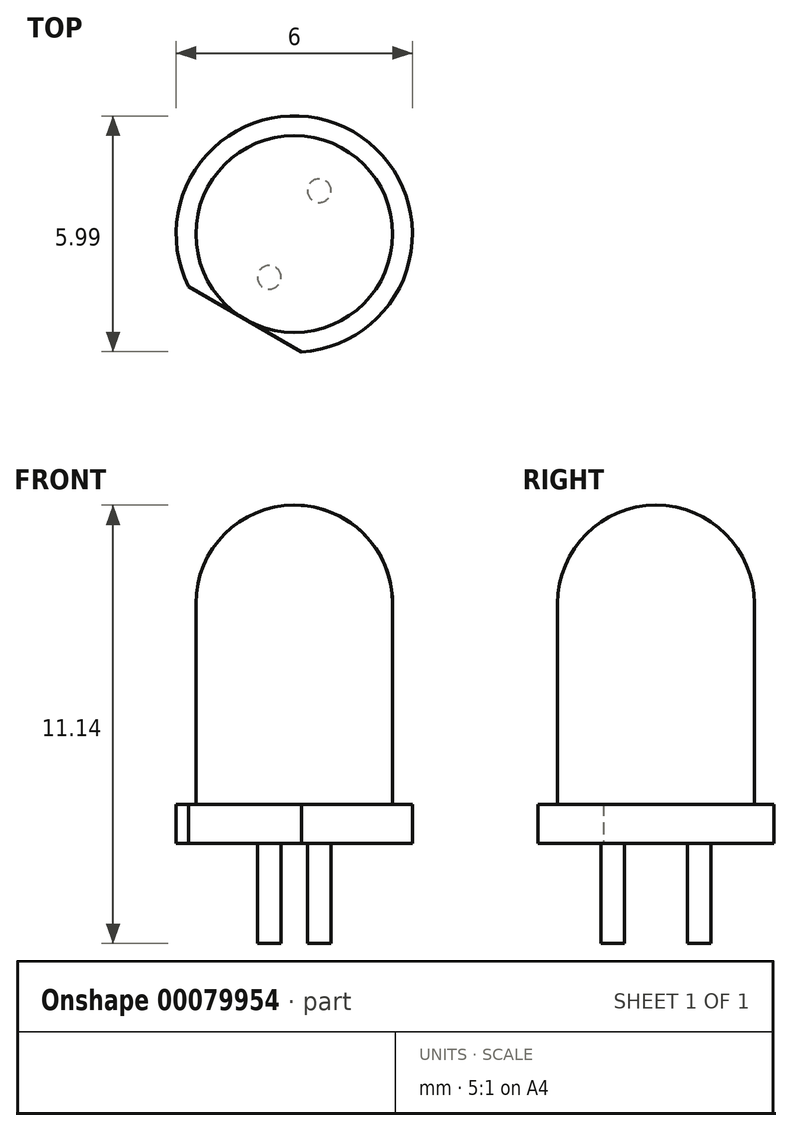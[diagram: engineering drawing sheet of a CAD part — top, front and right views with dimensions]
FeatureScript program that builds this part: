
annotation { "Feature Type Name" : "Feature", "Feature Type Description" : "" }
export const myFeature = defineFeature(function(context is Context, id is Id, definition is map)
    precondition{}
    {
        {
            var Q0;
            Q0=qCreatedBy(makeId("Top.planeOp"),FACE);
            var sketch = newSketch(context, id + "F0", { "sketchPlane" : qUnion([Q0])});
            skCircle(sketch, "E0", {"center": v(0, 0) * mm, "radius": 2.5 * mm});
            skCircle(sketch, "E1", {"center": v(0, 0) * mm, "radius": 3 * mm});
            skLineSegment(sketch, "E2", {"start": v(-1.27, 0) * mm, "end": v(1.27, 0) * mm});
            skCircle(sketch, "E3", {"center": v(-1.27, 0) * mm, "radius": 0.3 * mm});
            skCircle(sketch, "E4", {"center": v(1.27, 0) * mm, "radius": 0.3 * mm});
            skLineSegment(sketch, "E5", {"start": v(2.5, -1.66) * mm, "end": v(2.5, 1.66) * mm});
            skLineSegment(sketch, "E6", {"start": v(-2.69, -1.34) * mm, "end": v(0.18, -3) * mm});
            skLineSegment(sketch, "E7", {"start": v(-2.69, 1.34) * mm, "end": v(0.18, 3) * mm});
            skCircle(sketch, "E8", {"center": v(-0.64, -1.1) * mm, "radius": 0.3 * mm});
            skCircle(sketch, "E9", {"center": v(0.64, -1.1) * mm, "radius": 0.3 * mm});
            skCircle(sketch, "E10", {"center": v(0.64, 1.1) * mm, "radius": 0.3 * mm});
            skCircle(sketch, "E11", {"center": v(-0.64, 1.1) * mm, "radius": 0.3 * mm});
            skLineSegment(sketch, "E12", {"start": v(-0.64, -1.1) * mm, "end": v(-1.27, 0) * mm});
            skLineSegment(sketch, "E13", {"start": v(-0.64, -1.1) * mm, "end": v(0.64, -1.1) * mm});
            skLineSegment(sketch, "E14", {"start": v(0.63, -1.1) * mm, "end": v(1.27, 0) * mm});
            skLineSegment(sketch, "E15", {"start": v(1.27, 0) * mm, "end": v(0.63, 1.1) * mm});
            skLineSegment(sketch, "E16", {"start": v(-0.64, 1.1) * mm, "end": v(0.64, 1.1) * mm});
            skLineSegment(sketch, "E17", {"start": v(-0.64, 1.1) * mm, "end": v(-1.27, 0) * mm});
            skLineSegment(sketch, "E18", {"start": v(-0.64, -1.1) * mm, "end": v(0.64, 1.1) * mm});
            skLineSegment(sketch, "E19", {"start": v(-0.63, 1.1) * mm, "end": v(0.63, -1.1) * mm});
            skSolve(sketch);
        }
        {
            var Q0;
            Q0=makeQuery(id+"F0.imprint","IMPRINT",FACE,{"disambiguationData":[TD([[makeQuery(id+"F0.imprint","IMPRINT",EDGE,{"derivedFrom":sQuery(id+"F0.wireOp",EDGE,"E0")}),1.0]])]});
            var Q1;
            Q1=makeQuery(id+"F0.imprint","IMPRINT",FACE,{"disambiguationData":[TD([[makeQuery(id+"F0.imprint","IMPRINT",EDGE,{"derivedFrom":sQuery(id+"F0.wireOp",EDGE,"E3")}),1.0]])]});
            var Q2;
            Q2=makeQuery(id+"F0.imprint","IMPRINT",FACE,{"disambiguationData":[TD([[makeQuery(id+"F0.imprint","IMPRINT",EDGE,{"derivedFrom":sQuery(id+"F0.wireOp",EDGE,"E4")}),1.0]])]});
            var Q3;
            {var subQ5=sQuery(id+"F0.wireOp",EDGE,"E18");var subQ6=sQuery(id+"F0.wireOp",EDGE,"E8");var subQ7=makeQuery(id+"F0.imprint","INTERSECT",VERTEX,{"derivedFrom":[subQ6,subQ5]});Q3=makeQuery(id+"F0.imprint","IMPRINT",FACE,{"disambiguationData":[TD([[makeQuery(id+"F0.imprint","IMPRINT",EDGE,{"disambiguationData":[TD([[subQ7,1.0]])],"derivedFrom":subQ6}),-1.0]])]});}
            var Q4;
            {var subQ1=sQuery(id+"F0.wireOp",EDGE,"E3");var subQ7=sQuery(id+"F0.wireOp",EDGE,"E2");var subQ8=makeQuery(id+"F0.imprint","INTERSECT",VERTEX,{"derivedFrom":[subQ7,subQ1]});Q4=makeQuery(id+"F0.imprint","IMPRINT",FACE,{"disambiguationData":[TD([[makeQuery(id+"F0.imprint","IMPRINT",EDGE,{"disambiguationData":[TD([[subQ8,1.0]])],"derivedFrom":subQ1}),-1.0]])]});}
            var Q5;
            {var subQ0=sQuery(id+"F0.wireOp",EDGE,"E18");var subQ1=sQuery(id+"F0.wireOp",EDGE,"E8");var subQ2=makeQuery(id+"F0.imprint","INTERSECT",VERTEX,{"derivedFrom":[subQ1,subQ0]});Q5=makeQuery(id+"F0.imprint","IMPRINT",FACE,{"disambiguationData":[TD([[makeQuery(id+"F0.imprint","IMPRINT",EDGE,{"disambiguationData":[TD([[subQ2,-1.0]])],"derivedFrom":subQ1}),1.0]])]});}
            var Q6;
            {var subQ0=sQuery(id+"F0.wireOp",EDGE,"E13");var subQ1=sQuery(id+"F0.wireOp",EDGE,"E8");var subQ2=makeQuery(id+"F0.imprint","INTERSECT",VERTEX,{"derivedFrom":[subQ1,subQ0]});Q6=makeQuery(id+"F0.imprint","IMPRINT",FACE,{"disambiguationData":[TD([[makeQuery(id+"F0.imprint","IMPRINT",EDGE,{"disambiguationData":[TD([[subQ2,1.0]])],"derivedFrom":subQ1}),1.0]])]});}
            var Q7;
            {var subQ0=sQuery(id+"F0.wireOp",EDGE,"E18");var subQ1=sQuery(id+"F0.wireOp",EDGE,"E8");var subQ2=makeQuery(id+"F0.imprint","INTERSECT",VERTEX,{"derivedFrom":[subQ1,subQ0]});Q7=makeQuery(id+"F0.imprint","IMPRINT",FACE,{"disambiguationData":[TD([[makeQuery(id+"F0.imprint","IMPRINT",EDGE,{"disambiguationData":[TD([[subQ2,1.0]])],"derivedFrom":subQ1}),1.0]])]});}
            var Q8;
            {var subQ0=sQuery(id+"F0.wireOp",EDGE,"E19");var subQ1=sQuery(id+"F0.wireOp",EDGE,"E9");var subQ2=makeQuery(id+"F0.imprint","INTERSECT",VERTEX,{"derivedFrom":[subQ1,subQ0]});Q8=makeQuery(id+"F0.imprint","IMPRINT",FACE,{"disambiguationData":[TD([[makeQuery(id+"F0.imprint","IMPRINT",EDGE,{"disambiguationData":[TD([[subQ2,-1.0]])],"derivedFrom":subQ1}),1.0]])]});}
            var Q9;
            {var subQ0=sQuery(id+"F0.wireOp",EDGE,"E14");var subQ1=sQuery(id+"F0.wireOp",EDGE,"E9");var subQ2=makeQuery(id+"F0.imprint","INTERSECT",VERTEX,{"derivedFrom":[subQ1,subQ0]});Q9=makeQuery(id+"F0.imprint","IMPRINT",FACE,{"disambiguationData":[TD([[makeQuery(id+"F0.imprint","IMPRINT",EDGE,{"disambiguationData":[TD([[subQ2,1.0]])],"derivedFrom":subQ1}),1.0]])]});}
            var Q10;
            {var subQ0=sQuery(id+"F0.wireOp",EDGE,"E14");var subQ1=sQuery(id+"F0.wireOp",EDGE,"E9");var subQ2=makeQuery(id+"F0.imprint","INTERSECT",VERTEX,{"derivedFrom":[subQ1,subQ0]});Q10=makeQuery(id+"F0.imprint","IMPRINT",FACE,{"disambiguationData":[TD([[makeQuery(id+"F0.imprint","IMPRINT",EDGE,{"disambiguationData":[TD([[subQ2,1.0]])],"derivedFrom":subQ1}),1.0]])]});}
            var Q11;
            {var subQ0=sQuery(id+"F0.wireOp",EDGE,"E19");var subQ1=sQuery(id+"F0.wireOp",EDGE,"E9");var subQ2=makeQuery(id+"F0.imprint","INTERSECT",VERTEX,{"derivedFrom":[subQ1,subQ0]});Q11=makeQuery(id+"F0.imprint","IMPRINT",FACE,{"disambiguationData":[TD([[makeQuery(id+"F0.imprint","IMPRINT",EDGE,{"disambiguationData":[TD([[subQ2,1.0]])],"derivedFrom":subQ1}),1.0]])]});}
            var Q12;
            {var subQ1=sQuery(id+"F0.wireOp",EDGE,"E3");var subQ7=sQuery(id+"F0.wireOp",EDGE,"E2");var subQ9=makeQuery(id+"F0.imprint","INTERSECT",VERTEX,{"derivedFrom":[subQ7,subQ1]});Q12=makeQuery(id+"F0.imprint","IMPRINT",FACE,{"disambiguationData":[TD([[makeQuery(id+"F0.imprint","IMPRINT",EDGE,{"disambiguationData":[TD([[subQ9,-1.0]])],"derivedFrom":subQ1}),-1.0]])]});}
            var Q13;
            {var subQ0=sQuery(id+"F0.wireOp",EDGE,"E18");var subQ1=sQuery(id+"F0.wireOp",EDGE,"E10");var subQ2=makeQuery(id+"F0.imprint","INTERSECT",VERTEX,{"derivedFrom":[subQ1,subQ0]});Q13=makeQuery(id+"F0.imprint","IMPRINT",FACE,{"disambiguationData":[TD([[makeQuery(id+"F0.imprint","IMPRINT",EDGE,{"disambiguationData":[TD([[subQ2,1.0]])],"derivedFrom":subQ1}),-1.0]])]});}
            var Q14;
            {var subQ1=sQuery(id+"F0.wireOp",EDGE,"E4");var subQ7=sQuery(id+"F0.wireOp",EDGE,"E2");var subQ8=makeQuery(id+"F0.imprint","INTERSECT",VERTEX,{"derivedFrom":[subQ7,subQ1]});Q14=makeQuery(id+"F0.imprint","IMPRINT",FACE,{"disambiguationData":[TD([[makeQuery(id+"F0.imprint","IMPRINT",EDGE,{"disambiguationData":[TD([[subQ8,1.0]])],"derivedFrom":subQ1}),-1.0]])]});}
            var Q15;
            {var subQ1=sQuery(id+"F0.wireOp",EDGE,"E4");var subQ7=sQuery(id+"F0.wireOp",EDGE,"E2");var subQ9=makeQuery(id+"F0.imprint","INTERSECT",VERTEX,{"derivedFrom":[subQ7,subQ1]});Q15=makeQuery(id+"F0.imprint","IMPRINT",FACE,{"disambiguationData":[TD([[makeQuery(id+"F0.imprint","IMPRINT",EDGE,{"disambiguationData":[TD([[subQ9,-1.0]])],"derivedFrom":subQ1}),-1.0]])]});}
            var Q16;
            {var subQ0=sQuery(id+"F0.wireOp",EDGE,"E18");var subQ1=sQuery(id+"F0.wireOp",EDGE,"E10");var subQ2=makeQuery(id+"F0.imprint","INTERSECT",VERTEX,{"derivedFrom":[subQ1,subQ0]});Q16=makeQuery(id+"F0.imprint","IMPRINT",FACE,{"disambiguationData":[TD([[makeQuery(id+"F0.imprint","IMPRINT",EDGE,{"disambiguationData":[TD([[subQ2,-1.0]])],"derivedFrom":subQ1}),1.0]])]});}
            var Q17;
            {var subQ0=sQuery(id+"F0.wireOp",EDGE,"E18");var subQ1=sQuery(id+"F0.wireOp",EDGE,"E10");var subQ2=makeQuery(id+"F0.imprint","INTERSECT",VERTEX,{"derivedFrom":[subQ1,subQ0]});Q17=makeQuery(id+"F0.imprint","IMPRINT",FACE,{"disambiguationData":[TD([[makeQuery(id+"F0.imprint","IMPRINT",EDGE,{"disambiguationData":[TD([[subQ2,1.0]])],"derivedFrom":subQ1}),1.0]])]});}
            var Q18;
            {var subQ0=sQuery(id+"F0.wireOp",EDGE,"E16");var subQ1=sQuery(id+"F0.wireOp",EDGE,"E10");var subQ2=makeQuery(id+"F0.imprint","INTERSECT",VERTEX,{"derivedFrom":[subQ1,subQ0]});Q18=makeQuery(id+"F0.imprint","IMPRINT",FACE,{"disambiguationData":[TD([[makeQuery(id+"F0.imprint","IMPRINT",EDGE,{"disambiguationData":[TD([[subQ2,1.0]])],"derivedFrom":subQ1}),1.0]])]});}
            var Q19;
            {var subQ0=sQuery(id+"F0.wireOp",EDGE,"E17");var subQ1=sQuery(id+"F0.wireOp",EDGE,"E11");var subQ2=makeQuery(id+"F0.imprint","INTERSECT",VERTEX,{"derivedFrom":[subQ1,subQ0]});Q19=makeQuery(id+"F0.imprint","IMPRINT",FACE,{"disambiguationData":[TD([[makeQuery(id+"F0.imprint","IMPRINT",EDGE,{"disambiguationData":[TD([[subQ2,1.0]])],"derivedFrom":subQ1}),1.0]])]});}
            var Q20;
            {var subQ0=sQuery(id+"F0.wireOp",EDGE,"E17");var subQ1=sQuery(id+"F0.wireOp",EDGE,"E11");var subQ2=makeQuery(id+"F0.imprint","INTERSECT",VERTEX,{"derivedFrom":[subQ1,subQ0]});Q20=makeQuery(id+"F0.imprint","IMPRINT",FACE,{"disambiguationData":[TD([[makeQuery(id+"F0.imprint","IMPRINT",EDGE,{"disambiguationData":[TD([[subQ2,-1.0]])],"derivedFrom":subQ1}),1.0]])]});}
            var Q21;
            {var subQ0=sQuery(id+"F0.wireOp",EDGE,"E16");var subQ1=sQuery(id+"F0.wireOp",EDGE,"E11");var subQ2=makeQuery(id+"F0.imprint","INTERSECT",VERTEX,{"derivedFrom":[subQ1,subQ0]});Q21=makeQuery(id+"F0.imprint","IMPRINT",FACE,{"disambiguationData":[TD([[makeQuery(id+"F0.imprint","IMPRINT",EDGE,{"disambiguationData":[TD([[subQ2,1.0]])],"derivedFrom":subQ1}),1.0]])]});}
            extrude(context, id + "F1", {"entities" : qUnion([Q0, Q1, Q2, Q3, Q4, Q5, Q6, Q7, Q8, Q9, Q10, Q11, Q12, Q13, Q14, Q15, Q16, Q17, Q18, Q19, Q20, Q21]), "depth" : 8.6 * mm});
        }
        {
            var Q0;
            Q0=makeQuery(id+"F1.opExtrude","CAP_EDGE",EDGE,{"disambiguationData":[OSD([sQuery(id+"F0.wireOp",EDGE,"E0")])],"isStart":false});
            fillet(context, id + "F2", {"entities" : qUnion([Q0]), "radius" : 5 * mm / 2, "tangentPropagation" : true, "allowEdgeOverflow" : false});
        }
        {
            var Q0;
            {var subQ0=sQuery(id+"F0.wireOp",EDGE,"E0");Q0=makeQuery(id+"F0.imprint","IMPRINT",FACE,{"disambiguationData":[TD([[makeQuery(id+"F0.imprint","IMPRINT",EDGE,{"derivedFrom":subQ0}),-1.0]])]});}
            var Q1;
            {var subQ0=sQuery(id+"F0.wireOp",EDGE,"E7");Q1=makeQuery(id+"F0.imprint","IMPRINT",FACE,{"disambiguationData":[TD([[makeQuery(id+"F0.imprint","IMPRINT",EDGE,{"derivedFrom":subQ0}),1.0]])]});}
            var Q2;
            {var subQ0=sQuery(id+"F0.wireOp",EDGE,"E5");Q2=makeQuery(id+"F0.imprint","IMPRINT",FACE,{"disambiguationData":[TD([[makeQuery(id+"F0.imprint","IMPRINT",EDGE,{"derivedFrom":subQ0}),-1.0]])]});}
            extrude(context, id + "F3", {"entities" : qUnion([Q0, Q1, Q2]), "operationType" : NewBodyOperationType.ADD, "depth" : 1 * mm});
        }
        {
            var Q0;
            {var subQ0=sQuery(id+"F0.wireOp",EDGE,"E18");var subQ1=sQuery(id+"F0.wireOp",EDGE,"E8");var subQ2=makeQuery(id+"F0.imprint","INTERSECT",VERTEX,{"derivedFrom":[subQ1,subQ0]});Q0=makeQuery(id+"F0.imprint","IMPRINT",FACE,{"disambiguationData":[TD([[makeQuery(id+"F0.imprint","IMPRINT",EDGE,{"disambiguationData":[TD([[subQ2,-1.0]])],"derivedFrom":subQ1}),1.0]])]});}
            var Q1;
            {var subQ0=sQuery(id+"F0.wireOp",EDGE,"E13");var subQ1=sQuery(id+"F0.wireOp",EDGE,"E8");var subQ2=makeQuery(id+"F0.imprint","INTERSECT",VERTEX,{"derivedFrom":[subQ1,subQ0]});Q1=makeQuery(id+"F0.imprint","IMPRINT",FACE,{"disambiguationData":[TD([[makeQuery(id+"F0.imprint","IMPRINT",EDGE,{"disambiguationData":[TD([[subQ2,1.0]])],"derivedFrom":subQ1}),1.0]])]});}
            var Q2;
            {var subQ0=sQuery(id+"F0.wireOp",EDGE,"E18");var subQ1=sQuery(id+"F0.wireOp",EDGE,"E8");var subQ2=makeQuery(id+"F0.imprint","INTERSECT",VERTEX,{"derivedFrom":[subQ1,subQ0]});Q2=makeQuery(id+"F0.imprint","IMPRINT",FACE,{"disambiguationData":[TD([[makeQuery(id+"F0.imprint","IMPRINT",EDGE,{"disambiguationData":[TD([[subQ2,1.0]])],"derivedFrom":subQ1}),1.0]])]});}
            extrude(context, id + "F4", {"entities" : qUnion([Q0, Q1, Q2]), "operationType" : NewBodyOperationType.ADD, "oppositeDirection" : true, "depth" : 2.54 * mm});
        }
        {
            var Q0;
            {var subQ0=sQuery(id+"F0.wireOp",EDGE,"E16");var subQ1=sQuery(id+"F0.wireOp",EDGE,"E10");var subQ2=makeQuery(id+"F0.imprint","INTERSECT",VERTEX,{"derivedFrom":[subQ1,subQ0]});Q0=makeQuery(id+"F0.imprint","IMPRINT",FACE,{"disambiguationData":[TD([[makeQuery(id+"F0.imprint","IMPRINT",EDGE,{"disambiguationData":[TD([[subQ2,1.0]])],"derivedFrom":subQ1}),1.0]])]});}
            var Q1;
            {var subQ0=sQuery(id+"F0.wireOp",EDGE,"E18");var subQ1=sQuery(id+"F0.wireOp",EDGE,"E10");var subQ2=makeQuery(id+"F0.imprint","INTERSECT",VERTEX,{"derivedFrom":[subQ1,subQ0]});Q1=makeQuery(id+"F0.imprint","IMPRINT",FACE,{"disambiguationData":[TD([[makeQuery(id+"F0.imprint","IMPRINT",EDGE,{"disambiguationData":[TD([[subQ2,1.0]])],"derivedFrom":subQ1}),1.0]])]});}
            var Q2;
            {var subQ0=sQuery(id+"F0.wireOp",EDGE,"E18");var subQ1=sQuery(id+"F0.wireOp",EDGE,"E10");var subQ2=makeQuery(id+"F0.imprint","INTERSECT",VERTEX,{"derivedFrom":[subQ1,subQ0]});Q2=makeQuery(id+"F0.imprint","IMPRINT",FACE,{"disambiguationData":[TD([[makeQuery(id+"F0.imprint","IMPRINT",EDGE,{"disambiguationData":[TD([[subQ2,-1.0]])],"derivedFrom":subQ1}),1.0]])]});}
            extrude(context, id + "F5", {"entities" : qUnion([Q0, Q1, Q2]), "operationType" : NewBodyOperationType.ADD, "oppositeDirection" : true, "depth" : 2.54 * mm});
        }
    });
